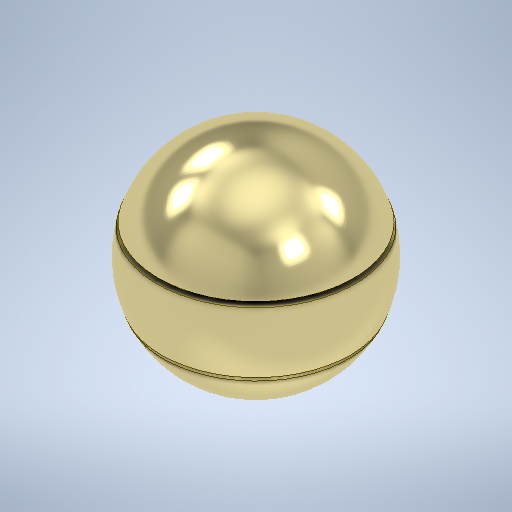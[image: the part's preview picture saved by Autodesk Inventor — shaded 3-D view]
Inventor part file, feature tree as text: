
AUTODESK INVENTOR PART (.ipt)
format: ipt  version: 2025.2 (Build 292293000, 293)  size: 314,368 bytes
history: native  units: mm
features: other x3, sketch x1
ambient origin geometry x8: Origin, YZ Plane, XZ Plane, XY Plane, X Axis, Y Axis, Z Axis, Center Point
bodies: Body1 (feature_tree)
feature tree (4):
  other  "Sólido1"
  sketch  "Esboço1"  dims[d0=20.0mm d4=360.0deg d6=2.0mm d7=25.0mm d8=0.5mm d9=0.5mm d10=180.0deg d5=0.872665mm d11=0.872665mm]
  other  "Revolução1"
  other  "Revolução2"
